# Revit family: BDG_BossDesign_Stng_TotoWIP28
name_source: partatom
category: Furniture
revit_build: Autodesk Revit 2016 (Build: 20150220_1215(x64)
units: mm (PartAtom-declared; Revit-internal decimal feet)

## family parameters
Always vertical = Yes
Cut with Voids When Loaded = No
Room Calculation Point = No
Shared = Yes
Work Plane-Based = No

## types (8) — shared parameters
Assembly Code = E2020200
AssetType = Movable
BIMObjectName = BDG_BossDesign_Seating_Toto
Category = Chairs, seats and benches : Pr_40_50_12
CodePerformance = BS EN 16139: 2013 Level 1 & 2
DurationUnit = year
ExpectedLife = 5
FrameMaterial = BDG_Generic_Metal_White
IfcExportAs = IfcFurnishingElementType
IfcExportType = CHAIR
Keynote = Pr_40_50_12
ManufacturerName = Boss Design
ManufacturerURL = www.bossdesign.com
NBSDescription = Seating
NBSReference = 45-35-72/352
Name = Seating_Toto_BossDesign
ProductInformation = www.bossdesign.com/product-list/toto
SeatMaterial = BDG_Camira_Fabric_Blazer_MidnightBlue
Shape = Rectangular
URL = www.bossdesign.com
Uniclass2015Code = Pr_40_50_12
Uniclass2015Title = Chairs, seats and benches
Uniclass2015Version = Products v1.10
Version = 1
WarrantyDurationLabor = 5
WarrantyDurationParts = 5
WarrantyDurationUnit = year

## per-type parameters (varying)
| type | Description | Features | Finish | Is4LegChromeFrame | Is4LegOakWhiteChassis | Is4StarBase | Is5StarBase | IsHighBackSeat | IsLowBackSeat | LegMaterial | Model | ModelNumber | ModelReference | NominalHeight | NominalLength | NominalWidth | Size |
| TOT1 Low Back Chair, 4-Leg Chrome Frame | Low Back Chair, 4-Leg Chrome Frame |  | Fully upholstered, Four Leg Chrome Frame | Yes | No | No | No | No | Yes | BDG_Generic_Metal_Chrome | TOT/1 | TOT/1 | Low Back Chair, 4-Leg Chrome Frame | 735 mm | 600 mm | 550 mm | 600 x 550 x 735mm |
| TOT2 High Back Chair, 4-Leg Chrome Frame | High Back Chair, 4-Leg Chrome Frame |  | Fully upholstered, Four Leg Chrome Frame | Yes | No | No | No | Yes | No | BDG_Generic_Metal_Chrome | TOT/2 | TOT/2 | High Back Chair, 4-Leg Chrome Frame | 805 mm | 600 mm | 595 mm | 600 x 595 x 805mm |
| TOT3 Low Back Chair, Polished 4-Star Base | Low Back Chair, Polished 4-Star Base |  | Fully upholstered, polished 4 star base | No | No | Yes | No | No | Yes | BDG_Generic_Metal_Aluminium_Polished | TOT/3 | TOT/3 | Low Back Chair, Polished 4-Star Base | 750 mm | 620 mm  [stored 2.03412 ft] | 550 mm | 620 x 550 x 750mm |
| TOT4 High Back Chair, Polished 4-Star Base | High Back Chair, Polished 4-Star Base |  | Fully upholstered, polished 4 star base | No | No | Yes | No | Yes | No | BDG_Generic_Metal_Aluminium_Polished | TOT/4 | TOT/4 | High Back Chair, Polished 4-Star Base | 820 mm | 600 mm | 575 mm | 600 x 575 x 820mm |
| TOT5 Low Back Chair, 4 Leg Oak, White Chassis | Low Back Chair, 4 Leg Oak, White Chassis |  | Fully upholstered 4-leg oak, white chassis | No | Yes | No | No | No | Yes | BDG_Generic_Wood_Oak | TOT/5 | TOT/5 | Low Back Chair, 4 Leg Oak, White Chassis | 745 mm | 620 mm  [stored 2.03412 ft] | 550 mm | 620 x 550 x 745mm |
| TOT6 High Back Chair, 4 Leg Oak, White Chassis | High Back Chair, 4 Leg Oak, White Chassis |  | Fully upholstered 4-leg oak, white chassis | No | Yes | No | No | Yes | No | BDG_Generic_Wood_Oak | TOT/6 | TOT/6 | High Back Chair, 4 Leg Oak, White Chassis | 820 mm | 600 mm | 585 mm | 600 x 585 x 820mm |
| TOT7 Low Back Chair, Polished 5-Star Base | Low Back Chair, Polished 5-Star Base | Height adjustable | Fully upholstered, polished 5 star base | No | No | No | Yes | No | Yes | BDG_Generic_Metal_Aluminium_Polished | TOT/7 | TOT/7 | Low Back Chair, Polished 5-Star Base | 815 mm | 700 mm | 675 mm | 700 x 675 x 815mm |
| TOT8 High Back Chair, Polished 5-Star Base | High Back Chair, Polished 5-Star Base | Height adjustable | Fully upholstered, polished 5 star base | No | No | No | Yes | Yes | No | BDG_Generic_Metal_Aluminium_Polished | TOT/8 | TOT/8 | High Back Chair, Polished 5-Star Base | 890 mm | 700 mm | 675 mm | 700 x 675 x 890mm |

note: [stored X ft] marks values corroborated as IEEE doubles in the binary element streams (Revit-internal decimal feet)

## geometry (parser evidence)
native form markers: Blend x2, Sweep x18
no freeform markers — native parametric forms only
